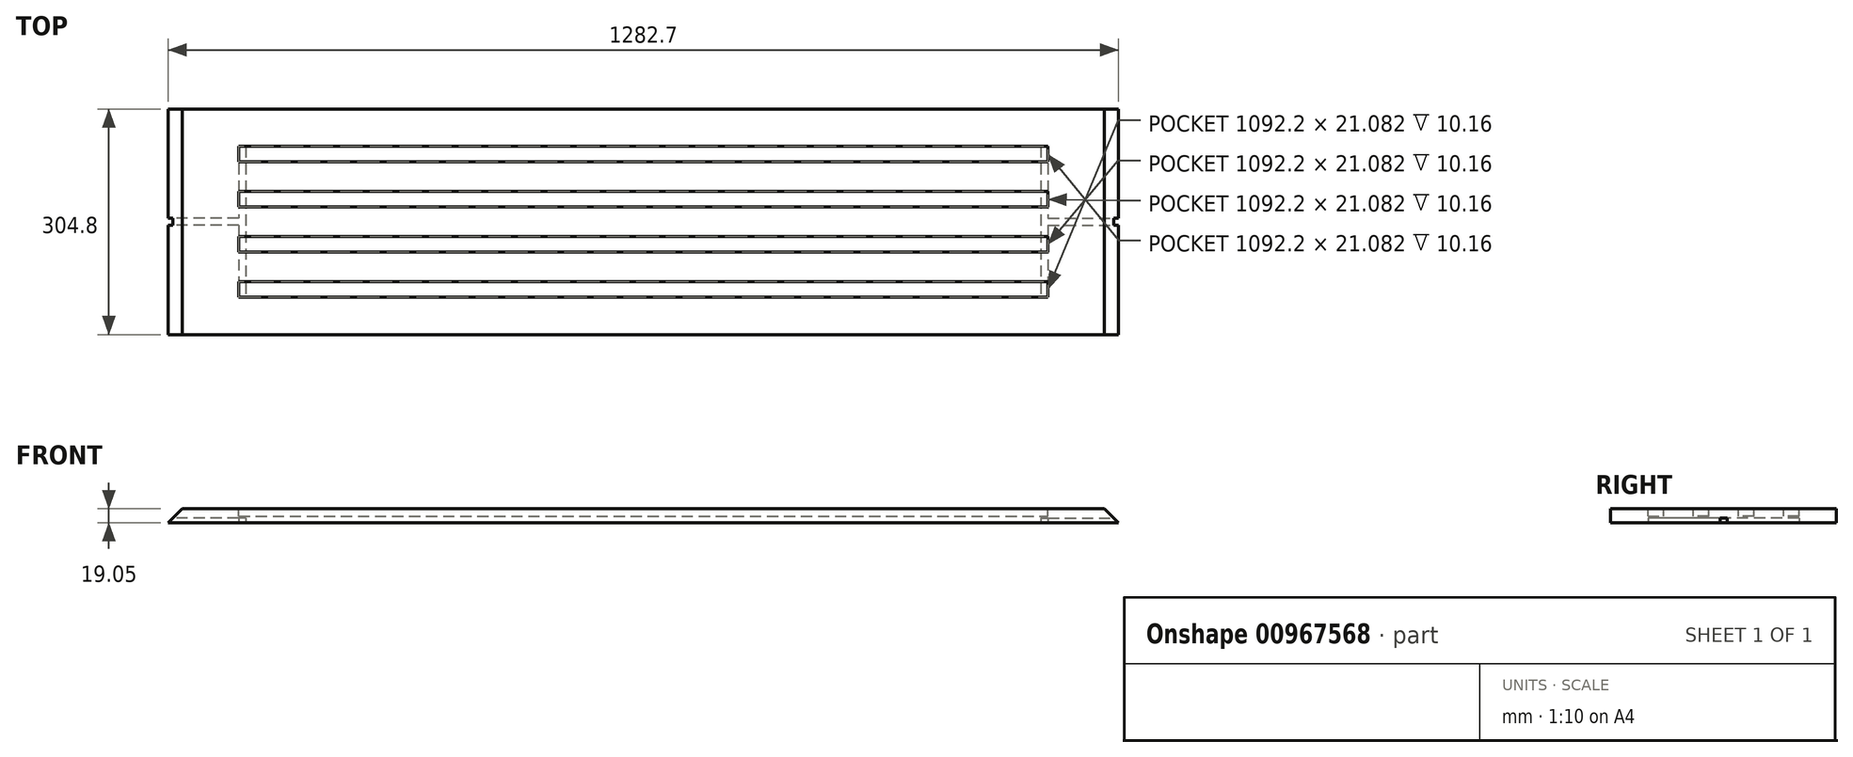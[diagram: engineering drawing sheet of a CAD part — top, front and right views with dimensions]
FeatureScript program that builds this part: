
annotation { "Feature Type Name" : "Feature", "Feature Type Description" : "" }
export const myFeature = defineFeature(function(context is Context, id is Id, definition is map)
    precondition{}
    {
        {
            var Q0;
            Q0=qCreatedBy(makeId("Top.planeOp"),FACE);
            var sketch = newSketch(context, id + "F0", { "sketchPlane" : qUnion([Q0])});
            skLineSegment(sketch, "E0.bottom", {"start": v(-278.56, 148.48) * mm, "end": v(1004.14, 148.48) * mm});
            skLineSegment(sketch, "E0.top", {"start": v(-278.56, -156.32) * mm, "end": v(1004.14, -156.32) * mm});
            skLineSegment(sketch, "E0.left", {"start": v(-278.56, 148.48) * mm, "end": v(-278.56, -156.32) * mm});
            skLineSegment(sketch, "E0.right", {"start": v(1004.14, 148.48) * mm, "end": v(1004.14, -156.32) * mm});
            skSolve(sketch);
        }
        {
            var Q0;
            Q0=makeQuery(id+"F0.imprint","IMPRINT",FACE,{"disambiguationData":[TD([[makeQuery(id+"F0.imprint","IMPRINT",EDGE,{"derivedFrom":sQuery(id+"F0.wireOp",EDGE,"E0.bottom")}),-1.0]])]});
            extrude(context, id + "F1", {"entities" : qUnion([Q0]), "depth" : 19.05 * mm, "offsetDistance" : 25.4 * mm});
        }
        {
            var Q0;
            Q0=makeQuery(id+"F1.opExtrude","CAP_EDGE",EDGE,{"disambiguationData":[OSD([sQuery(id+"F0.wireOp",EDGE,"E0.right")])],"isStart":false});
            var Q1;
            Q1=makeQuery(id+"F1.opExtrude","CAP_EDGE",EDGE,{"disambiguationData":[OSD([sQuery(id+"F0.wireOp",EDGE,"E0.left")])],"isStart":false});
            chamfer(context, id + "F2", {"entities" : qUnion([Q0, Q1]), "width" : 19.05 * mm});
        }
        {
            var Q0;
            Q0=makeQuery(id+"F1.opExtrude","CAP_FACE",FACE,{"disambiguationData":[OSD([sQuery(id+"F0.wireOp",EDGE,"E0.bottom"),sQuery(id+"F0.wireOp",EDGE,"E0.top"),sQuery(id+"F0.wireOp",EDGE,"E0.left"),sQuery(id+"F0.wireOp",EDGE,"E0.right")])],"isStart":false});
            var sketch = newSketch(context, id + "F3", { "sketchPlane" : qUnion([Q0])});
            skLineSegment(sketch, "E1", {"start": v(-259.5, 87.52) * mm, "end": v(985.1, 87.52) * mm, "construction": true});
            skLineSegment(sketch, "E2.bottom", {"start": v(-183.3, 98.06) * mm, "end": v(908.9, 98.06) * mm});
            skLineSegment(sketch, "E2.top", {"start": v(-183.3, 76.98) * mm, "end": v(908.9, 76.98) * mm});
            skLineSegment(sketch, "E2.left", {"start": v(-183.3, 98.06) * mm, "end": v(-183.3, 76.98) * mm});
            skLineSegment(sketch, "E2.right", {"start": v(908.9, 98.06) * mm, "end": v(908.9, 76.98) * mm});
            skLineSegment(sketch, "E3", {"start": v(-259.5, 26.56) * mm, "end": v(985.1, 26.56) * mm, "construction": true});
            skLineSegment(sketch, "E4.bottom", {"start": v(-183.3, 37.1) * mm, "end": v(908.9, 37.1) * mm});
            skLineSegment(sketch, "E4.top", {"start": v(-183.3, 16.02) * mm, "end": v(908.9, 16.02) * mm});
            skLineSegment(sketch, "E4.left", {"start": v(-183.3, 37.1) * mm, "end": v(-183.3, 16.02) * mm});
            skLineSegment(sketch, "E4.right", {"start": v(908.9, 37.1) * mm, "end": v(908.9, 16.02) * mm});
            skLineSegment(sketch, "E5", {"start": v(-259.5, -34.4) * mm, "end": v(985.1, -34.4) * mm, "construction": true});
            skLineSegment(sketch, "E6.bottom", {"start": v(-183.3, -23.86) * mm, "end": v(908.9, -23.86) * mm});
            skLineSegment(sketch, "E6.top", {"start": v(-183.3, -44.94) * mm, "end": v(908.9, -44.94) * mm});
            skLineSegment(sketch, "E6.left", {"start": v(-183.3, -23.86) * mm, "end": v(-183.3, -44.94) * mm});
            skLineSegment(sketch, "E6.right", {"start": v(908.9, -23.86) * mm, "end": v(908.9, -44.94) * mm});
            skLineSegment(sketch, "E7", {"start": v(-259.5, -95.36) * mm, "end": v(985.1, -95.36) * mm, "construction": true});
            skLineSegment(sketch, "E8.bottom", {"start": v(-183.3, -105.9) * mm, "end": v(908.9, -105.9) * mm});
            skLineSegment(sketch, "E8.top", {"start": v(-183.3, -84.82) * mm, "end": v(908.9, -84.82) * mm});
            skLineSegment(sketch, "E8.left", {"start": v(-183.3, -105.9) * mm, "end": v(-183.3, -84.82) * mm});
            skLineSegment(sketch, "E8.right", {"start": v(908.9, -105.9) * mm, "end": v(908.9, -84.82) * mm});
            skSolve(sketch);
        }
        {
            var Q0;
            Q0=makeQuery(id+"F3.imprint","IMPRINT",FACE,{"disambiguationData":[TD([[makeQuery(id+"F3.imprint","IMPRINT",EDGE,{"derivedFrom":sQuery(id+"F3.wireOp",EDGE,"E2.bottom")}),-1.0]])]});
            var Q1;
            Q1=makeQuery(id+"F3.imprint","IMPRINT",FACE,{"disambiguationData":[TD([[makeQuery(id+"F3.imprint","IMPRINT",EDGE,{"derivedFrom":sQuery(id+"F3.wireOp",EDGE,"E2.bottom")}),-1.0]])]});
            var Q2;
            Q2=makeQuery(id+"F3.imprint","IMPRINT",FACE,{"disambiguationData":[TD([[makeQuery(id+"F3.imprint","IMPRINT",EDGE,{"derivedFrom":sQuery(id+"F3.wireOp",EDGE,"E4.bottom")}),-1.0]])]});
            var Q3;
            Q3=makeQuery(id+"F3.imprint","IMPRINT",FACE,{"disambiguationData":[TD([[makeQuery(id+"F3.imprint","IMPRINT",EDGE,{"derivedFrom":sQuery(id+"F3.wireOp",EDGE,"E6.bottom")}),-1.0]])]});
            var Q4;
            Q4=makeQuery(id+"F3.imprint","IMPRINT",FACE,{"disambiguationData":[TD([[makeQuery(id+"F3.imprint","IMPRINT",EDGE,{"derivedFrom":sQuery(id+"F3.wireOp",EDGE,"E8.bottom")}),1.0]])]});
            extrude(context, id + "F4", {"entities" : qUnion([Q0, Q1, Q2, Q3, Q4]), "operationType" : NewBodyOperationType.REMOVE, "oppositeDirection" : true, "depth" : 10.16 * mm, "offsetDistance" : 25.4 * mm});
        }
        {
            var Q0;
            Q0=makeQuery(id+"F1.opExtrude","CAP_FACE",FACE,{"disambiguationData":[OSD([sQuery(id+"F0.wireOp",EDGE,"E0.bottom"),sQuery(id+"F0.wireOp",EDGE,"E0.top"),sQuery(id+"F0.wireOp",EDGE,"E0.left"),sQuery(id+"F0.wireOp",EDGE,"E0.right")])],"isStart":true});
            var Q1;
            Q1=makeQuery(id+"F1.opExtrude","CAP_FACE",FACE,{"disambiguationData":[OSD([sQuery(id+"F0.wireOp",EDGE,"E0.bottom"),sQuery(id+"F0.wireOp",EDGE,"E0.top"),sQuery(id+"F0.wireOp",EDGE,"E0.left"),sQuery(id+"F0.wireOp",EDGE,"E0.right")])],"isStart":true});
            var Q2;
            Q2=makeQuery(id+"F1.opExtrude","CAP_FACE",FACE,{"disambiguationData":[OSD([sQuery(id+"F0.wireOp",EDGE,"E0.bottom"),sQuery(id+"F0.wireOp",EDGE,"E0.top"),sQuery(id+"F0.wireOp",EDGE,"E0.left"),sQuery(id+"F0.wireOp",EDGE,"E0.right")])],"isStart":true});
            var sketch = newSketch(context, id + "F5", { "sketchPlane" : qUnion([Q0, Q1, Q2])});
            skLineSegment(sketch, "E9.bottom", {"start": v(899.37, -98.06) * mm, "end": v(908.9, -98.06) * mm});
            skLineSegment(sketch, "E9.top", {"start": v(899.37, 105.9) * mm, "end": v(908.9, 105.9) * mm});
            skLineSegment(sketch, "E9.left", {"start": v(899.37, -98.06) * mm, "end": v(899.37, 105.9) * mm});
            skLineSegment(sketch, "E9.right", {"start": v(908.9, -98.06) * mm, "end": v(908.9, -0.84) * mm});
            skLineSegment(sketch, "E10.bottom", {"start": v(908.9, -0.84) * mm, "end": v(1004.14, -0.84) * mm});
            skLineSegment(sketch, "E10.top", {"start": v(908.9, 8.69) * mm, "end": v(1004.14, 8.69) * mm});
            skLineSegment(sketch, "E10.right", {"start": v(1004.14, -0.84) * mm, "end": v(1004.14, 8.69) * mm});
            skLineSegment(sketch, "E11.trimOffspring", {"start": v(908.9, 8.69) * mm, "end": v(908.9, 105.9) * mm});
            skLineSegment(sketch, "E12", {"start": v(362.8, 266.51) * mm, "end": v(362.8, -315.33) * mm, "construction": true});
            skLineSegment(sketch, "E13.MirrorCS", {"start": v(-278.56, -0.84) * mm, "end": v(-278.56, 8.69) * mm});
            skLineSegment(sketch, "E14.MirrorCS", {"start": v(-173.78, -98.06) * mm, "end": v(-183.3, -98.06) * mm});
            skLineSegment(sketch, "E15.MirrorCS", {"start": v(-173.78, 105.9) * mm, "end": v(-183.3, 105.9) * mm});
            skLineSegment(sketch, "E16.MirrorCS", {"start": v(-183.3, 8.69) * mm, "end": v(-183.3, 105.9) * mm});
            skLineSegment(sketch, "E17.MirrorCS", {"start": v(-183.3, -0.84) * mm, "end": v(-278.56, -0.84) * mm});
            skLineSegment(sketch, "E18.MirrorCS", {"start": v(-183.3, 8.69) * mm, "end": v(-278.56, 8.69) * mm});
            skLineSegment(sketch, "E19.MirrorCS", {"start": v(-183.3, -98.06) * mm, "end": v(-183.3, -0.84) * mm});
            skLineSegment(sketch, "E20.MirrorCS", {"start": v(-173.78, -98.06) * mm, "end": v(-173.78, 105.9) * mm});
            skLineSegment(sketch, "E21", {"start": v(-304.79, 3.92) * mm, "end": v(1191.27, 3.92) * mm, "construction": true});
            skSolve(sketch);
        }
        {
            var Q0;
            Q0=makeQuery(id+"F5.imprint","IMPRINT",FACE,{"disambiguationData":[TD([[makeQuery(id+"F5.imprint","IMPRINT",EDGE,{"derivedFrom":sQuery(id+"F5.wireOp",EDGE,"E9.bottom")}),1.0]])]});
            var Q1;
            Q1=makeQuery(id+"F5.imprint","IMPRINT",FACE,{"disambiguationData":[TD([[makeQuery(id+"F5.imprint","IMPRINT",EDGE,{"derivedFrom":sQuery(id+"F5.wireOp",EDGE,"E13.MirrorCS")}),-1.0]])]});
            extrude(context, id + "F6", {"entities" : qUnion([Q0, Q1]), "operationType" : NewBodyOperationType.REMOVE, "oppositeDirection" : true, "depth" : 6.35 * mm, "offsetDistance" : 25.4 * mm});
        }
    });
